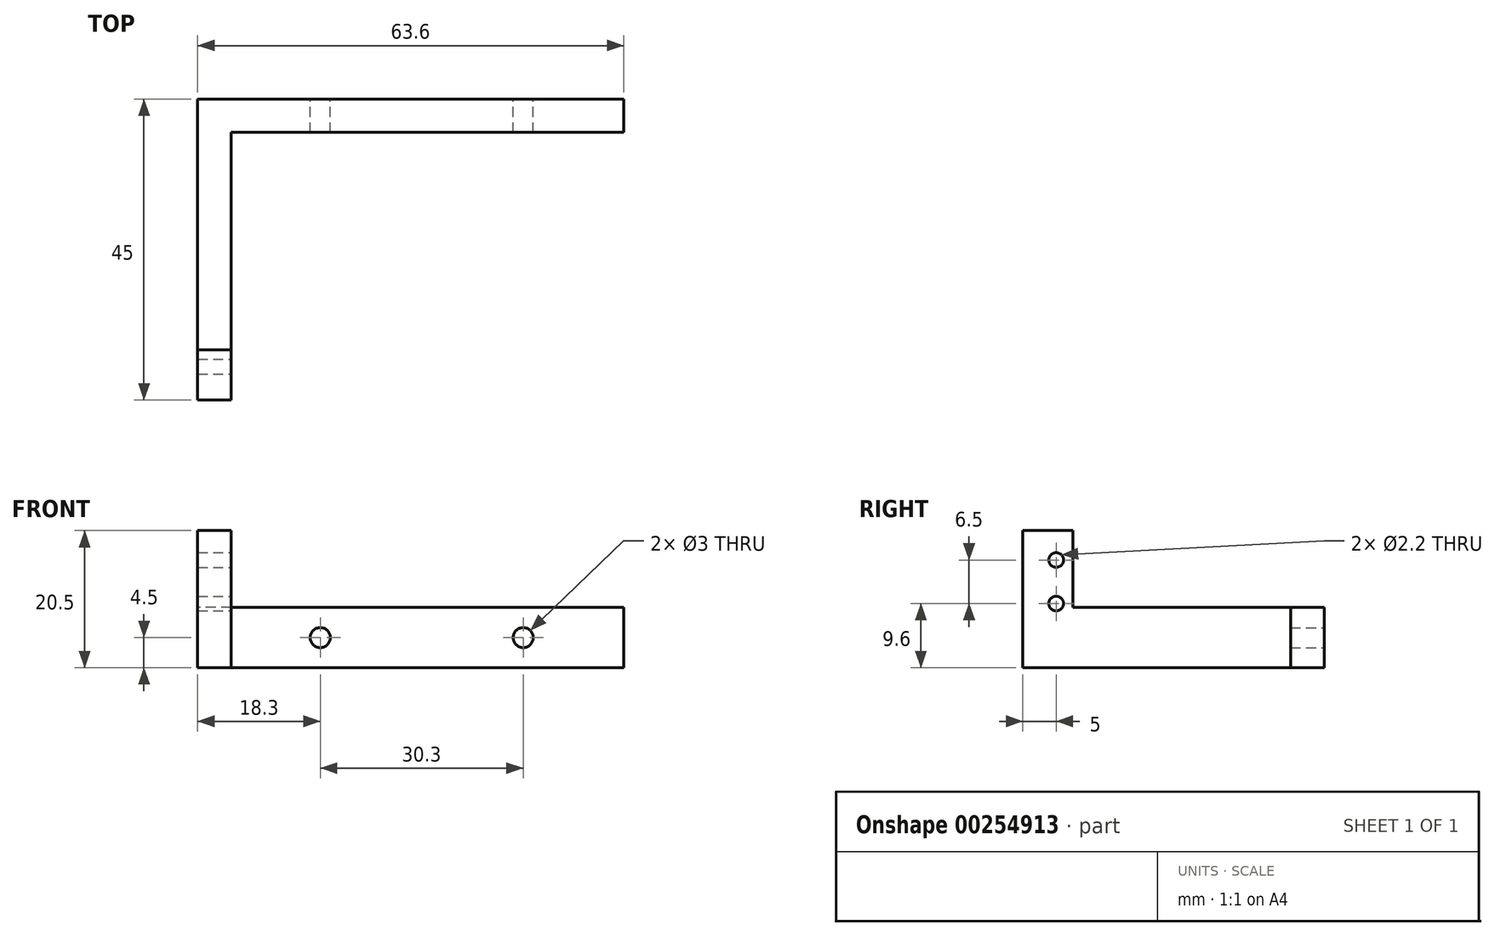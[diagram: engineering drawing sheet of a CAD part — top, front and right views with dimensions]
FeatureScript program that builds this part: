
annotation { "Feature Type Name" : "Feature", "Feature Type Description" : "" }
export const myFeature = defineFeature(function(context is Context, id is Id, definition is map)
    precondition{}
    {
        {
            var Q0;
            Q0=qCreatedBy(makeId("Front.planeOp"),FACE);
            var sketch = newSketch(context, id + "F0", { "sketchPlane" : qUnion([Q0])});
            skLineSegment(sketch, "E0.bottom", {"start": v(-31.8, -4.5) * mm, "end": v(31.8, -4.5) * mm});
            skLineSegment(sketch, "E0.top", {"start": v(-31.8, 4.5) * mm, "end": v(31.8, 4.5) * mm});
            skLineSegment(sketch, "E0.left", {"start": v(-31.8, -4.5) * mm, "end": v(-31.8, 4.5) * mm});
            skLineSegment(sketch, "E0.right", {"start": v(31.8, -4.5) * mm, "end": v(31.8, 4.5) * mm});
            skPoint(sketch, "E0.middle", {"position": v(0, 0) * mm});
            skCircle(sketch, "E1", {"center": v(-13.5, 0) * mm, "radius": 1.5 * mm});
            skCircle(sketch, "E2", {"center": v(16.8, 0) * mm, "radius": 1.5 * mm});
            skSolve(sketch);
        }
        {
            var Q0;
            Q0 = qSketchRegion(id + "F0", true);
            extrude(context, id + "F1", {"entities" : qUnion([Q0]), "depth" : 5 * mm});
        }
        {
            var Q0;
            Q0=makeQuery(id+"F1.opExtrude","CAP_FACE",FACE,{"disambiguationData":[OSD([sQuery(id+"F0.wireOp",EDGE,"E0.bottom"),sQuery(id+"F0.wireOp",EDGE,"E0.top"),sQuery(id+"F0.wireOp",EDGE,"E0.left"),sQuery(id+"F0.wireOp",EDGE,"E0.right"),sQuery(id+"F0.wireOp",EDGE,"E1"),sQuery(id+"F0.wireOp",EDGE,"E2")])],"isStart":false});
            var sketch = newSketch(context, id + "F2", { "sketchPlane" : qUnion([Q0])});
            skLineSegment(sketch, "E3.bottom", {"start": v(-31.8, 4.5) * mm, "end": v(-26.8, 4.5) * mm});
            skLineSegment(sketch, "E3.top", {"start": v(-31.8, -4.5) * mm, "end": v(-26.8, -4.5) * mm});
            skLineSegment(sketch, "E3.left", {"start": v(-31.8, 4.5) * mm, "end": v(-31.8, -4.5) * mm});
            skLineSegment(sketch, "E3.right", {"start": v(-26.8, 4.5) * mm, "end": v(-26.8, -4.5) * mm});
            skSolve(sketch);
        }
        {
            var Q0;
            Q0 = qSketchRegion(id + "F2", true);
            extrude(context, id + "F3", {"entities" : qUnion([Q0]), "operationType" : NewBodyOperationType.ADD, "depth" : 40 * mm});
        }
        {
            var Q0;
            Q0=makeQuery(id+"F3.boolean.opBoolean","MERGE",FACE,{"derivedFrom":[makeQuery(id+"F1.opExtrude","SWEPT_FACE",FACE,{"disambiguationData":[OSD([sQuery(id+"F0.wireOp",EDGE,"E0.top")])]}),makeQuery(id+"F3.opExtrude","SWEPT_FACE",FACE,{"disambiguationData":[OSD([sQuery(id+"F2.wireOp",EDGE,"E3.bottom")])]})]});
            var sketch = newSketch(context, id + "F4", { "sketchPlane" : qUnion([Q0])});
            skLineSegment(sketch, "E4.bottom", {"start": v(-26.8, -45) * mm, "end": v(-31.8, -45) * mm});
            skLineSegment(sketch, "E4.top", {"start": v(-26.8, -37.5) * mm, "end": v(-31.8, -37.5) * mm});
            skLineSegment(sketch, "E4.left", {"start": v(-26.8, -45) * mm, "end": v(-26.8, -37.5) * mm});
            skLineSegment(sketch, "E4.right", {"start": v(-31.8, -45) * mm, "end": v(-31.8, -37.5) * mm});
            skSolve(sketch);
        }
        {
            var Q0;
            Q0 = qSketchRegion(id + "F4", true);
            extrude(context, id + "F5", {"entities" : qUnion([Q0]), "operationType" : NewBodyOperationType.ADD, "depth" : 11.5 * mm});
        }
        {
            var Q0;
            Q0=makeQuery(id+"F5.boolean.opBoolean","MERGE",FACE,{"derivedFrom":[makeQuery(id+"F3.opExtrude","SWEPT_FACE",FACE,{"disambiguationData":[OSD([sQuery(id+"F2.wireOp",EDGE,"E3.right")])]}),makeQuery(id+"F5.opExtrude","SWEPT_FACE",FACE,{"disambiguationData":[OSD([sQuery(id+"F4.wireOp",EDGE,"E4.left")])]})]});
            var sketch = newSketch(context, id + "F6", { "sketchPlane" : qUnion([Q0])});
            skCircle(sketch, "E5", {"center": v(-40, 5.1) * mm, "radius": 1.1 * mm});
            skCircle(sketch, "E6", {"center": v(-40, 11.6) * mm, "radius": 1.1 * mm});
            skSolve(sketch);
        }
        {
            var Q0;
            Q0 = qSketchRegion(id + "F6", true);
            extrude(context, id + "F7", {"entities" : qUnion([Q0]), "operationType" : NewBodyOperationType.REMOVE, "endBound" : BoundingType.THROUGH_ALL, "oppositeDirection" : true, "depth" : 25 * mm});
        }
    });
